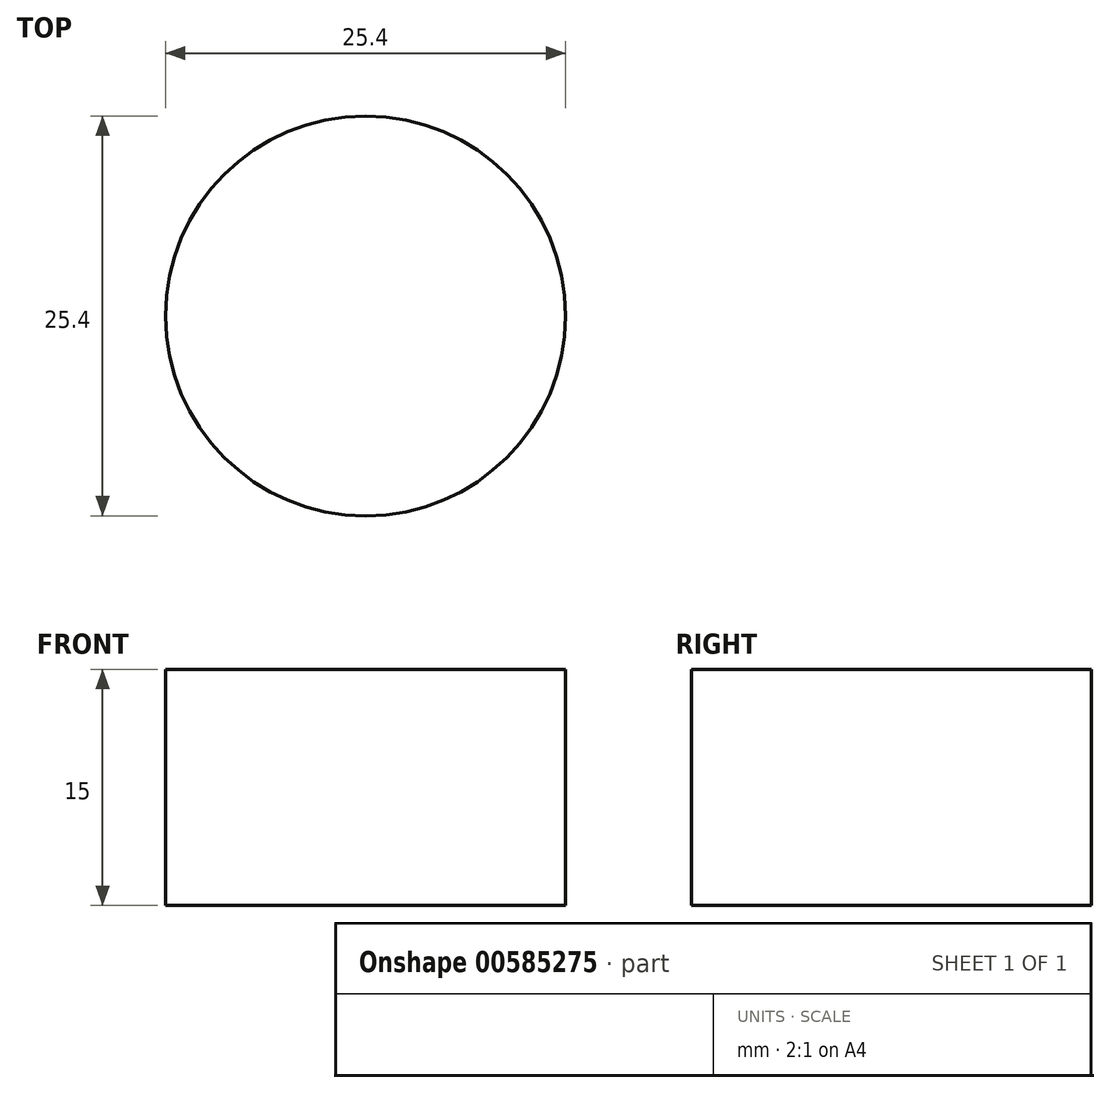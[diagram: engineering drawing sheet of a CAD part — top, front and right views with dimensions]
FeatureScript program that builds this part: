
annotation { "Feature Type Name" : "Feature", "Feature Type Description" : "" }
export const myFeature = defineFeature(function(context is Context, id is Id, definition is map)
    precondition{}
    {
        {
            var Q0;
            Q0=qCreatedBy(makeId("Top.planeOp"),FACE);
            var sketch = newSketch(context, id + "F0", { "sketchPlane" : qUnion([Q0])});
            skCircle(sketch, "E0", {"center": v(-32.17, 12.76) * mm, "radius": 12.7 * mm});
            skSolve(sketch);
        }
        {
            var Q0;
            Q0 = qSketchRegion(id + "F0", true);
            extrude(context, id + "F1", {"entities" : qUnion([Q0]), "depth" : 15 * mm, "offsetDistance" : 25.4 * mm});
        }
    });
